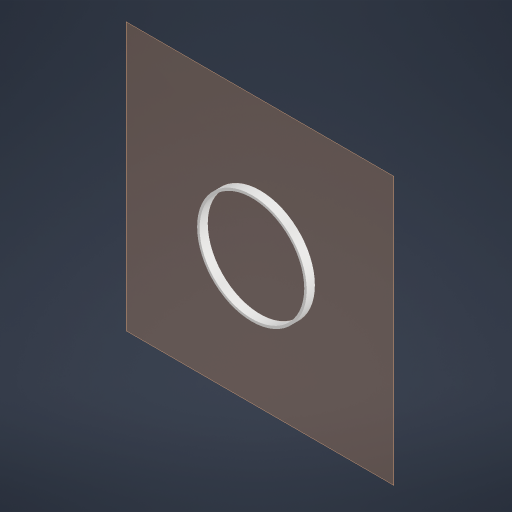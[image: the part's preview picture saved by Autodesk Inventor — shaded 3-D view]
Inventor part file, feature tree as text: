
AUTODESK INVENTOR PART (.ipt)
format: ipt  version: 2023.1 (Build 271208000, 208)  size: 176,128 bytes
history: native  units: mm
features: other x3, plane x1, extrude x1, sketch x1
ambient origin geometry x8: Origin, YZ Plane, XZ Plane, XY Plane, X Axis, Y Axis, Z Axis, Center Point
bodies: Solid1 (feature_tree)
feature tree (6):
  plane  "Work Plane1"
  extrude  "Extrusion1"  Depth=10.0mm
  sketch  "Sketch1"  dims[d0=127.323954mm d1=3.0mm d2=10.0mm d3=0.0mm]
  parser-record x1  (decoder bookkeeping rows leaked as tree rows — omitted from the tree; the rows remain in map.json)
  other  "Beau4tClock.iam"
  other  "Clock:1"
note: 1 file-system path scrubbed to <path> (originals preserved in map.json)
